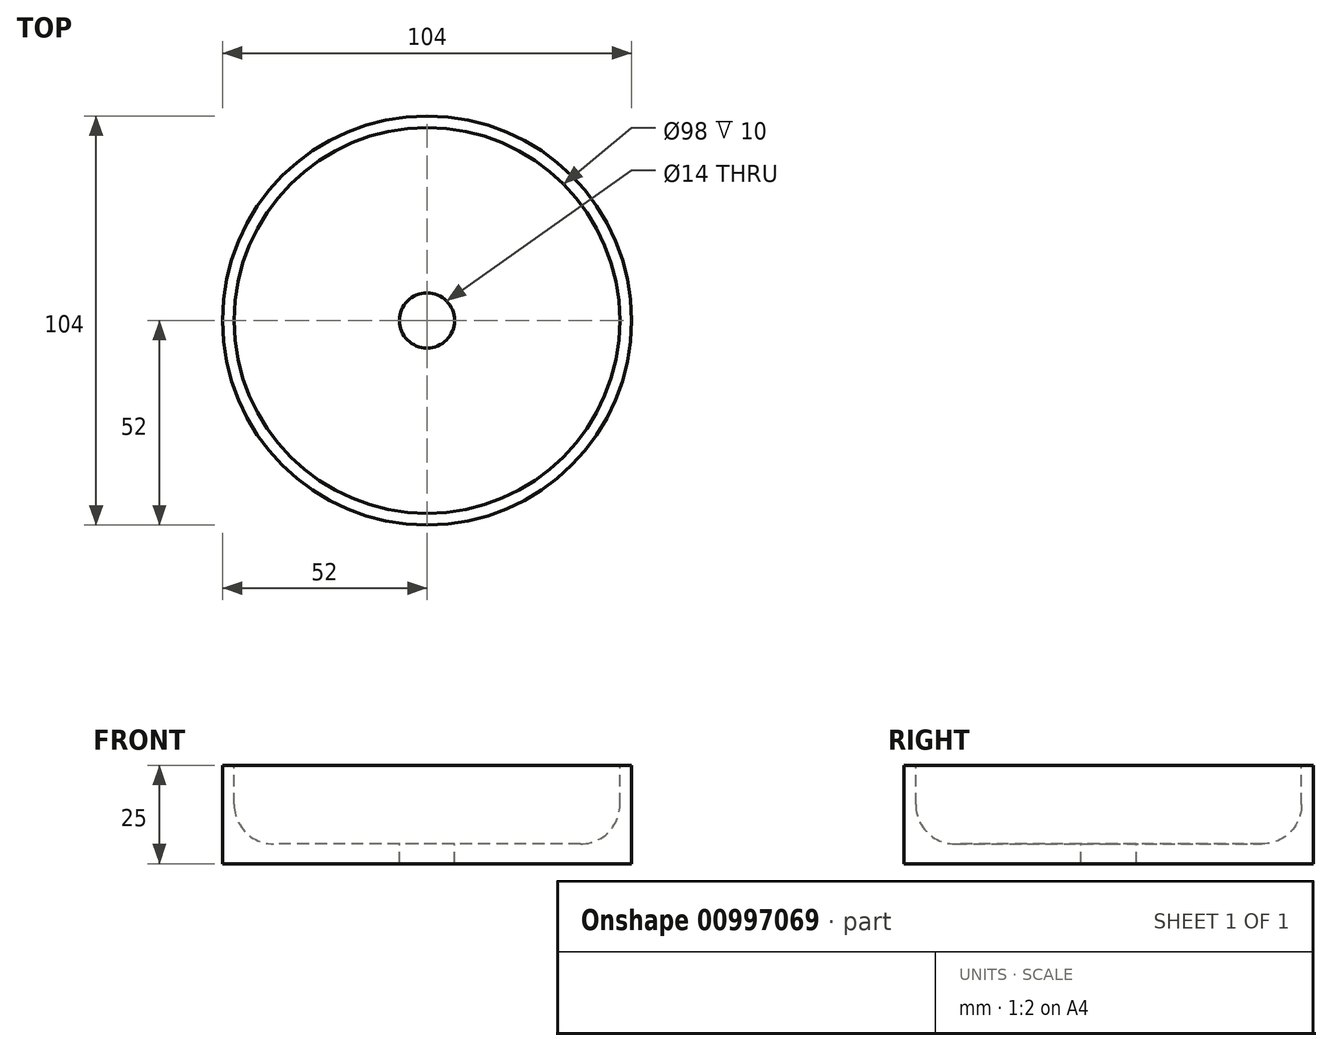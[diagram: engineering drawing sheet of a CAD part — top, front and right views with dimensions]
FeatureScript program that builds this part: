
annotation { "Feature Type Name" : "Feature", "Feature Type Description" : "" }
export const myFeature = defineFeature(function(context is Context, id is Id, definition is map)
    precondition{}
    {
        {
            var Q0;
            Q0=qCreatedBy(makeId("Front.planeOp"),FACE);
            var sketch = newSketch(context, id + "F0", { "sketchPlane" : qUnion([Q0])});
            skLineSegment(sketch, "E0", {"start": v(0, 5) * mm, "end": v(-39, 5) * mm});
            skLineSegment(sketch, "E1", {"start": v(-49, 15) * mm, "end": v(-49, 25) * mm});
            skLineSegment(sketch, "E2", {"start": v(-49, 25) * mm, "end": v(-52, 25) * mm});
            skLineSegment(sketch, "E3", {"start": v(-52, 25) * mm, "end": v(-52, 0) * mm});
            skLineSegment(sketch, "E4", {"start": v(-52, 0) * mm, "end": v(0, 0) * mm});
            skLineSegment(sketch, "E5", {"start": v(0, 0) * mm, "end": v(0, 5) * mm});
            skLineSegment(sketch, "E6", {"start": v(0, 63.2) * mm, "end": v(0, -58.47) * mm, "construction": true});
            skPoint(sketch, "E7.visualSharp", {"position": v(-49, 5) * mm});
            skArc(sketch, "E7.filletArc", {"start": v(-49, 15) * mm, "mid": v(-46.07, 7.93) * mm, "end": v(-39, 5) * mm});
            skSolve(sketch);
        }
        {
            var Q0;
            Q0 = qSketchRegion(id + "F0", true);
            var Q1;
            Q1=sQuery(id+"F0.wireOp",EDGE,"E6");
            revolve(context, id + "F1", {"surfaceOperationType" : NewSurfaceOperationType.NEW, "entities" : qUnion([Q0]), "axis" : qUnion([Q1]), "revolveType" : RevolveType.FULL});
        }
        {
            var Q0;
            Q0=makeQuery(id+"F1.opRevolve","SWEPT_FACE",FACE,{"disambiguationData":[OSD([sQuery(id+"F0.wireOp",EDGE,"E0")])]});
            var sketch = newSketch(context, id + "F2", { "sketchPlane" : qUnion([Q0])});
            skCircle(sketch, "E8", {"center": v(0, 0) * mm, "radius": 7 * mm});
            skSolve(sketch);
        }
        {
            var Q0;
            Q0 = qSketchRegion(id + "F2", true);
            var Q1;
            Q1=sQuery(id+"F2.wireOp",EDGE,"E8");
            extrude(context, id + "F3", {"entities" : qUnion([Q0]), "operationType" : NewBodyOperationType.REMOVE, "surfaceOperationType" : NewSurfaceOperationType.ADD, "surfaceEntities" : qUnion([Q1]), "oppositeDirection" : true, "depth" : 25 * mm, "offsetDistance" : 25 * mm});
        }
    });
